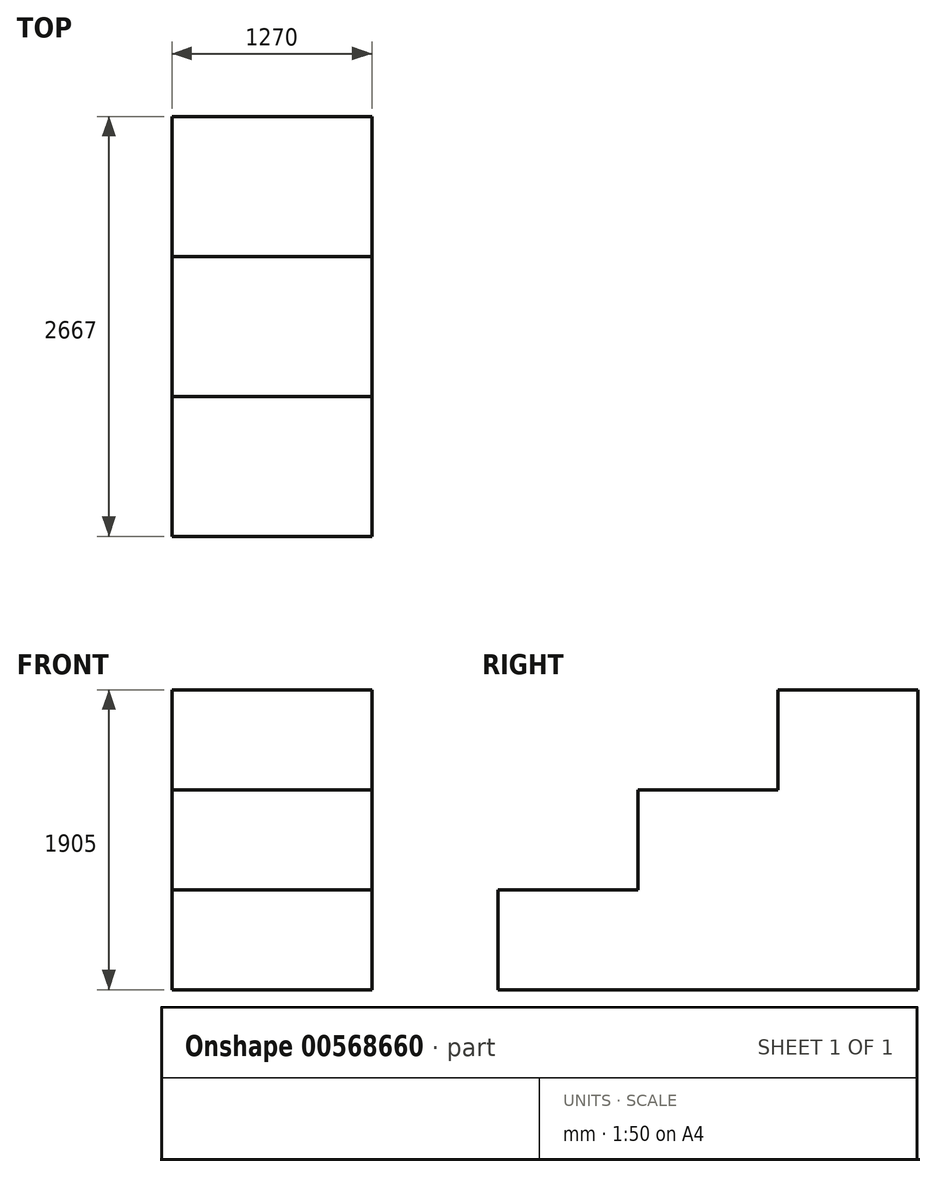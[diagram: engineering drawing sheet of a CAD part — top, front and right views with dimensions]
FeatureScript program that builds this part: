
annotation { "Feature Type Name" : "Feature", "Feature Type Description" : "" }
export const myFeature = defineFeature(function(context is Context, id is Id, definition is map)
    precondition{}
    {
        {
            var Q0;
            Q0=qCreatedBy(makeId("Right.planeOp"),FACE);
            var sketch = newSketch(context, id + "F0", { "sketchPlane" : qUnion([Q0])});
            skLineSegment(sketch, "E0", {"start": v(0, 0) * mm, "end": v(-2667, 0) * mm});
            skLineSegment(sketch, "E1", {"start": v(-2667, 0) * mm, "end": v(-2667, 635) * mm});
            skLineSegment(sketch, "E2", {"start": v(-2667, 635) * mm, "end": v(-1778, 635) * mm});
            skLineSegment(sketch, "E3", {"start": v(-1778, 635) * mm, "end": v(-1778, 1270) * mm});
            skLineSegment(sketch, "E4", {"start": v(-1778, 1270) * mm, "end": v(-889, 1270) * mm});
            skLineSegment(sketch, "E5", {"start": v(-889, 1270) * mm, "end": v(-889, 1905) * mm});
            skLineSegment(sketch, "E6", {"start": v(-889, 1905) * mm, "end": v(0, 1905) * mm});
            skLineSegment(sketch, "E7", {"start": v(0, 1905) * mm, "end": v(0, 0) * mm});
            skSolve(sketch);
        }
        {
            var Q0;
            Q0 = qSketchRegion(id + "F0", true);
            extrude(context, id + "F1", {"entities" : qUnion([Q0]), "depth" : 1270 * mm, "offsetDistance" : 25.4 * mm});
        }
    });
